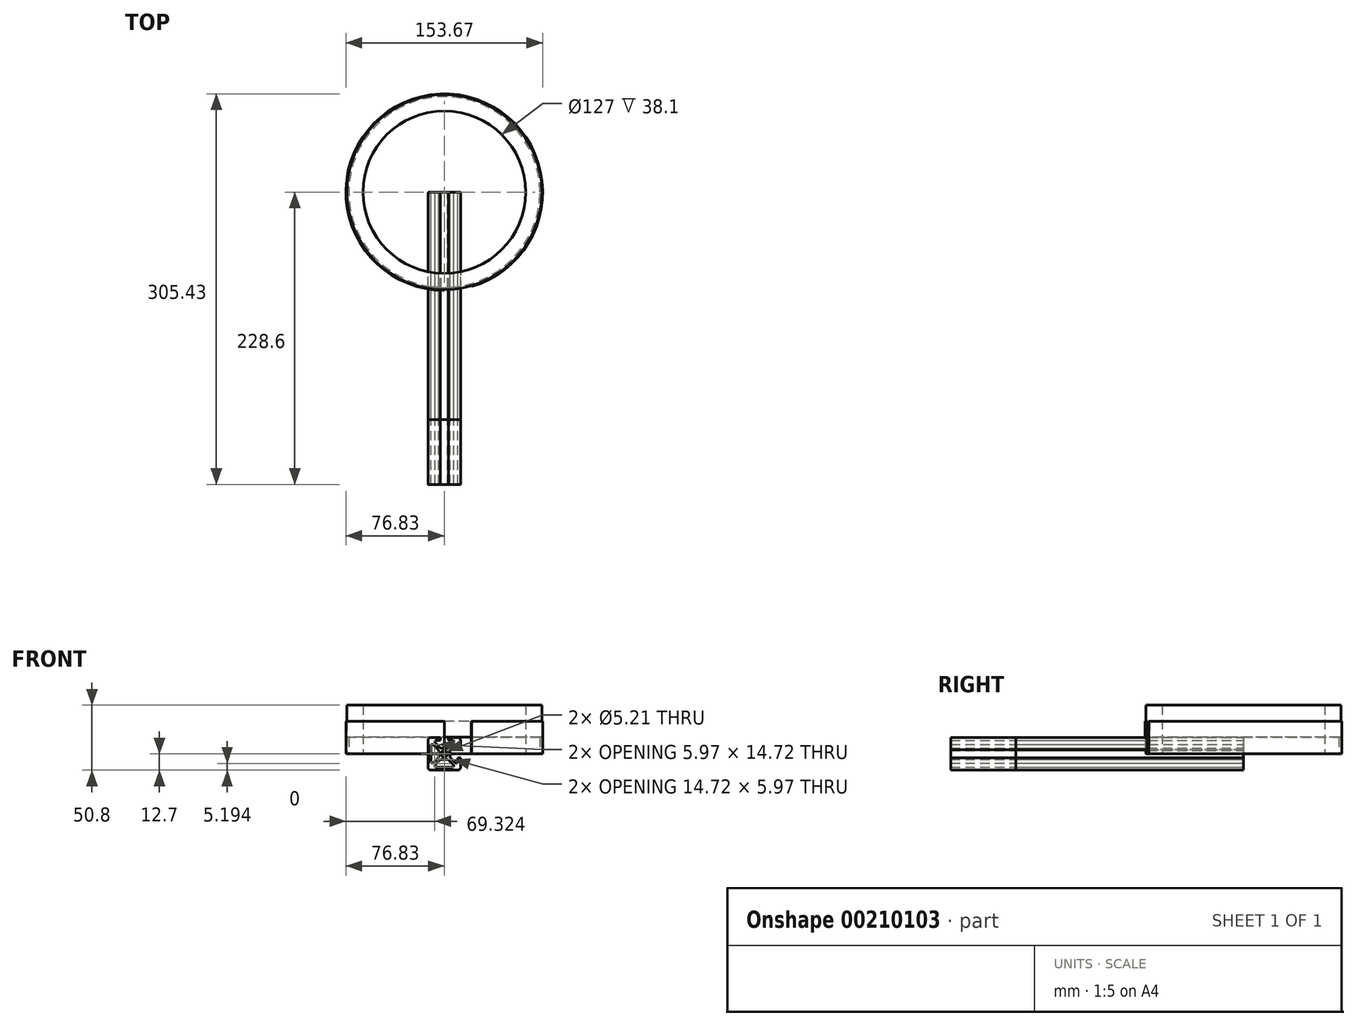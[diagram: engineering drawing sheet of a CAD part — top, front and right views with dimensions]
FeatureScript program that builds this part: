
annotation { "Feature Type Name" : "Feature", "Feature Type Description" : "" }
export const myFeature = defineFeature(function(context is Context, id is Id, definition is map)
    precondition{}
    {
        {
            var Q0;
            Q0=qCreatedBy(makeId("Front.planeOp"),FACE);
            var sketch = newSketch(context, id + "F0", { "sketchPlane" : qUnion([Q0])});
            skLineSegment(sketch, "E0.bottom", {"start": v(10.5, 12.7) * mm, "end": v(-10.5, 12.7) * mm});
            skLineSegment(sketch, "E0.top", {"start": v(10.5, -12.7) * mm, "end": v(-10.5, -12.7) * mm});
            skLineSegment(sketch, "E0.left", {"start": v(12.7, 10.5) * mm, "end": v(12.7, -10.5) * mm});
            skLineSegment(sketch, "E0.right", {"start": v(-12.7, 10.5) * mm, "end": v(-12.7, -10.5) * mm});
            skPoint(sketch, "E0.middle", {"position": v(0, 0) * mm});
            skCircle(sketch, "E1", {"center": v(0, 0) * mm, "radius": 2.6 * mm});
            skPoint(sketch, "E2.visualSharp", {"position": v(12.7, 12.7) * mm});
            skArc(sketch, "E2.filletArc", {"start": v(12.7, 10.5) * mm, "mid": v(12.05, 12.05) * mm, "end": v(10.5, 12.7) * mm});
            skPoint(sketch, "E3.visualSharp", {"position": v(-12.7, 12.7) * mm});
            skArc(sketch, "E3.filletArc", {"start": v(-10.5, 12.7) * mm, "mid": v(-12.05, 12.05) * mm, "end": v(-12.7, 10.5) * mm});
            skPoint(sketch, "E4.visualSharp", {"position": v(-12.7, -12.7) * mm});
            skArc(sketch, "E4.filletArc", {"start": v(-12.7, -10.5) * mm, "mid": v(-12.05, -12.05) * mm, "end": v(-10.5, -12.7) * mm});
            skPoint(sketch, "E5.visualSharp", {"position": v(12.7, -12.7) * mm});
            skArc(sketch, "E5.filletArc", {"start": v(10.5, -12.7) * mm, "mid": v(12.05, -12.05) * mm, "end": v(12.7, -10.5) * mm});
            skLineSegment(sketch, "E6.0", {"start": v(-3.28, 4.84) * mm, "end": v(-7.04, 8.6) * mm});
            skLineSegment(sketch, "E7", {"start": v(-2.5, 4.52) * mm, "end": v(2.5, 4.52) * mm});
            skLineSegment(sketch, "E8.MirrorCS", {"start": v(3.28, 4.84) * mm, "end": v(7.04, 8.6) * mm});
            skLineSegment(sketch, "E9", {"start": v(-6.26, 10.5) * mm, "end": v(6.26, 10.5) * mm});
            skPoint(sketch, "E10.newPointA", {"position": v(-7.42, 10.5) * mm});
            skPoint(sketch, "E10.newPointB", {"position": v(-9.7, 11.27) * mm});
            skArc(sketch, "E10.filletArc", {"start": v(-6.26, 10.5) * mm, "mid": v(-7.28, 9.8) * mm, "end": v(-7.04, 8.6) * mm});
            skPoint(sketch, "E11.newPointA", {"position": v(7.42, 10.5) * mm});
            skPoint(sketch, "E11.newPointB", {"position": v(9.7, 11.27) * mm});
            skArc(sketch, "E11.filletArc", {"start": v(7.04, 8.6) * mm, "mid": v(7.28, 9.8) * mm, "end": v(6.26, 10.5) * mm});
            skPoint(sketch, "E12.newPointA", {"position": v(-4.52, 4.52) * mm});
            skPoint(sketch, "E12.newPointB", {"position": v(0.78, 0.78) * mm});
            skArc(sketch, "E12.filletArc", {"start": v(-3.28, 4.84) * mm, "mid": v(-2.92, 4.6) * mm, "end": v(-2.5, 4.52) * mm});
            skPoint(sketch, "E13.newPointA", {"position": v(4.52, 4.52) * mm});
            skPoint(sketch, "E13.newPointB", {"position": v(-0.78, 0.78) * mm});
            skArc(sketch, "E13.filletArc", {"start": v(2.5, 4.52) * mm, "mid": v(2.92, 4.6) * mm, "end": v(3.28, 4.84) * mm});
            skArc(sketch, "E14.1.0", {"start": v(-10.5, -6.26) * mm, "mid": v(-9.8, -7.28) * mm, "end": v(-8.6, -7.04) * mm});
            skPoint(sketch, "E14.1.1", {"position": v(-10.5, -7.42) * mm});
            skPoint(sketch, "E14.1.3", {"position": v(-4.52, -4.52) * mm});
            skArc(sketch, "E14.1.4", {"start": v(-4.84, -3.28) * mm, "mid": v(-4.6, -2.92) * mm, "end": v(-4.52, -2.5) * mm});
            skLineSegment(sketch, "E14.1.5", {"start": v(-4.52, -2.5) * mm, "end": v(-4.52, 2.5) * mm});
            skLineSegment(sketch, "E14.1.6", {"start": v(-4.84, -3.28) * mm, "end": v(-8.6, -7.04) * mm});
            skArc(sketch, "E14.1.7", {"start": v(-8.6, 7.04) * mm, "mid": v(-9.8, 7.28) * mm, "end": v(-10.5, 6.26) * mm});
            skArc(sketch, "E14.1.8", {"start": v(-4.52, 2.5) * mm, "mid": v(-4.6, 2.92) * mm, "end": v(-4.84, 3.28) * mm});
            skLineSegment(sketch, "E14.1.9", {"start": v(-10.5, -6.26) * mm, "end": v(-10.5, 6.26) * mm});
            skLineSegment(sketch, "E14.1.10", {"start": v(-4.84, 3.28) * mm, "end": v(-8.6, 7.04) * mm});
            skPoint(sketch, "E14.1.11", {"position": v(-10.5, 7.42) * mm});
            skArc(sketch, "E14.2.0", {"start": v(6.26, -10.5) * mm, "mid": v(7.28, -9.8) * mm, "end": v(7.04, -8.6) * mm});
            skPoint(sketch, "E14.2.1", {"position": v(7.42, -10.5) * mm});
            skPoint(sketch, "E14.2.2", {"position": v(-4.52, -4.52) * mm});
            skPoint(sketch, "E14.2.3", {"position": v(4.52, -4.52) * mm});
            skArc(sketch, "E14.2.4", {"start": v(3.28, -4.84) * mm, "mid": v(2.92, -4.6) * mm, "end": v(2.5, -4.52) * mm});
            skLineSegment(sketch, "E14.2.5", {"start": v(2.5, -4.52) * mm, "end": v(-2.5, -4.52) * mm});
            skLineSegment(sketch, "E14.2.6", {"start": v(3.28, -4.84) * mm, "end": v(7.04, -8.6) * mm});
            skArc(sketch, "E14.2.7", {"start": v(-7.04, -8.6) * mm, "mid": v(-7.28, -9.8) * mm, "end": v(-6.26, -10.5) * mm});
            skArc(sketch, "E14.2.8", {"start": v(-2.5, -4.52) * mm, "mid": v(-2.92, -4.6) * mm, "end": v(-3.28, -4.84) * mm});
            skLineSegment(sketch, "E14.2.9", {"start": v(6.26, -10.5) * mm, "end": v(-6.26, -10.5) * mm});
            skLineSegment(sketch, "E14.2.10", {"start": v(-3.28, -4.84) * mm, "end": v(-7.04, -8.6) * mm});
            skPoint(sketch, "E14.2.11", {"position": v(-7.42, -10.5) * mm});
            skArc(sketch, "E14.3.0", {"start": v(10.5, 6.26) * mm, "mid": v(9.8, 7.28) * mm, "end": v(8.6, 7.04) * mm});
            skPoint(sketch, "E14.3.1", {"position": v(10.5, 7.42) * mm});
            skPoint(sketch, "E14.3.2", {"position": v(4.52, -4.52) * mm});
            skArc(sketch, "E14.3.4", {"start": v(4.84, 3.28) * mm, "mid": v(4.6, 2.92) * mm, "end": v(4.52, 2.5) * mm});
            skLineSegment(sketch, "E14.3.5", {"start": v(4.52, 2.5) * mm, "end": v(4.52, -2.5) * mm});
            skLineSegment(sketch, "E14.3.6", {"start": v(4.84, 3.28) * mm, "end": v(8.6, 7.04) * mm});
            skArc(sketch, "E14.3.7", {"start": v(8.6, -7.04) * mm, "mid": v(9.8, -7.28) * mm, "end": v(10.5, -6.26) * mm});
            skArc(sketch, "E14.3.8", {"start": v(4.52, -2.5) * mm, "mid": v(4.6, -2.92) * mm, "end": v(4.84, -3.28) * mm});
            skLineSegment(sketch, "E14.3.9", {"start": v(10.5, 6.26) * mm, "end": v(10.5, -6.26) * mm});
            skLineSegment(sketch, "E14.3.10", {"start": v(4.84, -3.28) * mm, "end": v(8.6, -7.04) * mm});
            skPoint(sketch, "E14.3.11", {"position": v(10.5, -7.42) * mm});
            skLineSegment(sketch, "E15.bottom", {"start": v(3.25, 17.01) * mm, "end": v(-3.25, 17.01) * mm});
            skLineSegment(sketch, "E15.top", {"start": v(3.25, 8.39) * mm, "end": v(-3.25, 8.39) * mm});
            skLineSegment(sketch, "E15.left", {"start": v(3.25, 17.01) * mm, "end": v(3.25, 8.39) * mm});
            skLineSegment(sketch, "E15.right", {"start": v(-3.25, 17.01) * mm, "end": v(-3.25, 8.39) * mm});
            skPoint(sketch, "E15.middle", {"position": v(0, 12.7) * mm});
            skLineSegment(sketch, "E16.bottom", {"start": v(7.75, -3.25) * mm, "end": v(17.65, -3.25) * mm});
            skLineSegment(sketch, "E16.top", {"start": v(7.75, 3.25) * mm, "end": v(17.65, 3.25) * mm});
            skLineSegment(sketch, "E16.left", {"start": v(7.75, -3.25) * mm, "end": v(7.75, 3.25) * mm});
            skLineSegment(sketch, "E16.right", {"start": v(17.65, -3.25) * mm, "end": v(17.65, 3.25) * mm});
            skPoint(sketch, "E16.middle", {"position": v(12.7, 0) * mm});
            skSolve(sketch);
        }
        {
            var Q0;
            Q0=makeQuery(id+"F0.imprint","IMPRINT",FACE,{"disambiguationData":[TD([[makeQuery(id+"F0.imprint","IMPRINT",EDGE,{"derivedFrom":sQuery(id+"F0.wireOp",EDGE,"E0.bottom")}),1.0]])]});
            extrude(context, id + "F1", {"entities" : qUnion([Q0]), "depth" : 228.6 * mm});
        }
        {
            var Q0;
            Q0=qCreatedBy(makeId("Front.planeOp"),FACE);
            var sketch = newSketch(context, id + "F2", { "sketchPlane" : qUnion([Q0])});
            skLineSegment(sketch, "E17.bottom", {"start": v(10.5, 12.7) * mm, "end": v(-10.5, 12.7) * mm});
            skLineSegment(sketch, "E17.top", {"start": v(10.5, -12.7) * mm, "end": v(-10.5, -12.7) * mm});
            skLineSegment(sketch, "E17.left", {"start": v(12.7, 10.5) * mm, "end": v(12.7, -10.5) * mm});
            skLineSegment(sketch, "E17.right", {"start": v(-12.7, 10.5) * mm, "end": v(-12.7, -10.5) * mm});
            skPoint(sketch, "E17.middle", {"position": v(0, 0) * mm});
            skCircle(sketch, "E18", {"center": v(0, 0) * mm, "radius": 2.6 * mm});
            skPoint(sketch, "E19.visualSharp", {"position": v(12.7, 12.7) * mm});
            skArc(sketch, "E19.filletArc", {"start": v(12.7, 10.5) * mm, "mid": v(12.05, 12.05) * mm, "end": v(10.5, 12.7) * mm});
            skPoint(sketch, "E20.visualSharp", {"position": v(-12.7, 12.7) * mm});
            skArc(sketch, "E20.filletArc", {"start": v(-10.5, 12.7) * mm, "mid": v(-12.05, 12.05) * mm, "end": v(-12.7, 10.5) * mm});
            skPoint(sketch, "E21.visualSharp", {"position": v(-12.7, -12.7) * mm});
            skArc(sketch, "E21.filletArc", {"start": v(-12.7, -10.5) * mm, "mid": v(-12.05, -12.05) * mm, "end": v(-10.5, -12.7) * mm});
            skPoint(sketch, "E22.visualSharp", {"position": v(12.7, -12.7) * mm});
            skArc(sketch, "E22.filletArc", {"start": v(10.5, -12.7) * mm, "mid": v(12.05, -12.05) * mm, "end": v(12.7, -10.5) * mm});
            skSolve(sketch);
        }
        {
            var Q0;
            Q0=makeQuery(id+"F2.imprint","IMPRINT",FACE,{"disambiguationData":[TD([[makeQuery(id+"F2.imprint","IMPRINT",EDGE,{"derivedFrom":sQuery(id+"F2.wireOp",EDGE,"E17.bottom")}),1.0]])]});
            extrude(context, id + "F3", {"entities" : qUnion([Q0]), "depth" : 177.8 * mm});
        }
        {
            var Q0;
            Q0=makeQuery(id+"F0.imprint","IMPRINT",FACE,{"disambiguationData":[TD([[makeQuery(id+"F0.imprint","IMPRINT",EDGE,{"derivedFrom":sQuery(id+"F0.wireOp",EDGE,"E6.0")}),-1.0]])]});
            var Q1;
            Q1=makeQuery(id+"F0.imprint","IMPRINT",FACE,{"disambiguationData":[TD([[makeQuery(id+"F0.imprint","IMPRINT",EDGE,{"derivedFrom":sQuery(id+"F0.wireOp",EDGE,"E14.1.0")}),1.0]])]});
            var Q2;
            Q2=makeQuery(id+"F0.imprint","IMPRINT",FACE,{"disambiguationData":[TD([[makeQuery(id+"F0.imprint","IMPRINT",EDGE,{"derivedFrom":sQuery(id+"F0.wireOp",EDGE,"E14.3.0")}),1.0]])]});
            var Q3;
            Q3=makeQuery(id+"F0.imprint","IMPRINT",FACE,{"disambiguationData":[TD([[makeQuery(id+"F0.imprint","IMPRINT",EDGE,{"derivedFrom":sQuery(id+"F0.wireOp",EDGE,"E14.2.0")}),1.0]])]});
            extrude(context, id + "F4", {"entities" : qUnion([Q0, Q1, Q2, Q3]), "operationType" : NewBodyOperationType.REMOVE, "endBound" : BoundingType.THROUGH_ALL, "depth" : 25.4 * mm});
        }
        {
            var Q0;
            {var subQ0=sQuery(id+"F0.wireOp",EDGE,"E15.left");var subQ1=sQuery(id+"F0.wireOp",EDGE,"E0.bottom");var subQ2=makeQuery(id+"F0.imprint","INTERSECT",VERTEX,{"derivedFrom":[subQ1,subQ0]});Q0=makeQuery(id+"F0.imprint","IMPRINT",FACE,{"disambiguationData":[TD([[makeQuery(id+"F0.imprint","IMPRINT",EDGE,{"disambiguationData":[TD([[subQ2,-1.0]])],"derivedFrom":subQ1}),1.0]])]});}
            var Q1;
            {var subQ5=sQuery(id+"F0.wireOp",EDGE,"E15.top");Q1=makeQuery(id+"F0.imprint","IMPRINT",FACE,{"disambiguationData":[TD([[makeQuery(id+"F0.imprint","IMPRINT",EDGE,{"derivedFrom":subQ5}),-1.0]])]});}
            var Q2;
            {var subQ5=sQuery(id+"F0.wireOp",EDGE,"E15.bottom");Q2=makeQuery(id+"F0.imprint","IMPRINT",FACE,{"disambiguationData":[TD([[makeQuery(id+"F0.imprint","IMPRINT",EDGE,{"derivedFrom":subQ5}),1.0]])]});}
            extrude(context, id + "F5", {"entities" : qUnion([Q0, Q1, Q2]), "operationType" : NewBodyOperationType.REMOVE, "endBound" : BoundingType.THROUGH_ALL, "depth" : 25.4 * mm});
        }
        {
            var Q0;
            {var subQ5=sQuery(id+"F0.wireOp",EDGE,"E16.right");Q0=makeQuery(id+"F0.imprint","IMPRINT",FACE,{"disambiguationData":[TD([[makeQuery(id+"F0.imprint","IMPRINT",EDGE,{"derivedFrom":subQ5}),1.0]])]});}
            var Q1;
            {var subQ0=sQuery(id+"F0.wireOp",EDGE,"E16.top");var subQ1=sQuery(id+"F0.wireOp",EDGE,"E0.left");var subQ2=makeQuery(id+"F0.imprint","INTERSECT",VERTEX,{"derivedFrom":[subQ1,subQ0]});Q1=makeQuery(id+"F0.imprint","IMPRINT",FACE,{"disambiguationData":[TD([[makeQuery(id+"F0.imprint","IMPRINT",EDGE,{"disambiguationData":[TD([[subQ2,-1.0]])],"derivedFrom":subQ1}),-1.0]])]});}
            var Q2;
            {var subQ5=sQuery(id+"F0.wireOp",EDGE,"E16.left");Q2=makeQuery(id+"F0.imprint","IMPRINT",FACE,{"disambiguationData":[TD([[makeQuery(id+"F0.imprint","IMPRINT",EDGE,{"derivedFrom":subQ5}),-1.0]])]});}
            extrude(context, id + "F6", {"entities" : qUnion([Q0, Q1, Q2]), "operationType" : NewBodyOperationType.REMOVE, "endBound" : BoundingType.THROUGH_ALL, "depth" : 25.4 * mm});
        }
        {
            var Q0;
            Q0=makeQuery(id+"F5.boolean.opBoolean","INTERSECT",EDGE,{"derivedFrom":[makeQuery(id+"F3.opExtrude","SWEPT_FACE",FACE,{"disambiguationData":[OSD([sQuery(id+"F2.wireOp",EDGE,"E17.bottom")])]}),makeQuery(id+"F5.opExtrude","SWEPT_FACE",FACE,{"disambiguationData":[OSD([sQuery(id+"F0.wireOp",EDGE,"E15.right")])]})]});
            var Q1;
            Q1=makeQuery(id+"F4.boolean.opBoolean","COPY",EDGE,{"derivedFrom":makeQuery(id+"F4.opExtrude","SWEPT_EDGE",EDGE,{"disambiguationData":[OSD([sQuery(id+"F0.wireOp",EDGE,"E9"),sQuery(id+"F0.wireOp",EDGE,"E15.right")])]})});
            var Q2;
            Q2=makeQuery(id+"F5.boolean.opBoolean","INTERSECT",EDGE,{"derivedFrom":[makeQuery(id+"F3.opExtrude","SWEPT_FACE",FACE,{"disambiguationData":[OSD([sQuery(id+"F2.wireOp",EDGE,"E17.bottom")])]}),makeQuery(id+"F5.opExtrude","SWEPT_FACE",FACE,{"disambiguationData":[OSD([sQuery(id+"F0.wireOp",EDGE,"E15.left")])]})]});
            var Q3;
            Q3=makeQuery(id+"F6.boolean.opBoolean","INTERSECT",EDGE,{"derivedFrom":[makeQuery(id+"F3.opExtrude","SWEPT_FACE",FACE,{"disambiguationData":[OSD([sQuery(id+"F2.wireOp",EDGE,"E17.left")])]}),makeQuery(id+"F6.opExtrude","SWEPT_FACE",FACE,{"disambiguationData":[OSD([sQuery(id+"F0.wireOp",EDGE,"E16.top")])]})]});
            var Q4;
            Q4=makeQuery(id+"F6.boolean.opBoolean","INTERSECT",EDGE,{"derivedFrom":[makeQuery(id+"F3.opExtrude","SWEPT_FACE",FACE,{"disambiguationData":[OSD([sQuery(id+"F2.wireOp",EDGE,"E17.left")])]}),makeQuery(id+"F6.opExtrude","SWEPT_FACE",FACE,{"disambiguationData":[OSD([sQuery(id+"F0.wireOp",EDGE,"E16.bottom")])]})]});
            var Q5;
            Q5=makeQuery(id+"F4.boolean.opBoolean","COPY",EDGE,{"derivedFrom":makeQuery(id+"F4.opExtrude","SWEPT_EDGE",EDGE,{"disambiguationData":[OSD([sQuery(id+"F0.wireOp",EDGE,"E14.3.9"),sQuery(id+"F0.wireOp",EDGE,"E16.bottom")])]})});
            var Q6;
            Q6=makeQuery(id+"F4.boolean.opBoolean","COPY",EDGE,{"derivedFrom":makeQuery(id+"F4.opExtrude","SWEPT_EDGE",EDGE,{"disambiguationData":[OSD([sQuery(id+"F0.wireOp",EDGE,"E9"),sQuery(id+"F0.wireOp",EDGE,"E15.left")])]})});
            var Q7;
            Q7=makeQuery(id+"F4.boolean.opBoolean","COPY",EDGE,{"derivedFrom":makeQuery(id+"F4.opExtrude","SWEPT_EDGE",EDGE,{"disambiguationData":[OSD([sQuery(id+"F0.wireOp",EDGE,"E14.3.9"),sQuery(id+"F0.wireOp",EDGE,"E16.top")])]})});
            fillet(context, id + "F7", {"entities" : qUnion([Q0, Q1, Q2, Q3, Q4, Q5, Q6, Q7]), "radius" : 1.1 * mm, "tangentPropagation" : true, "allowEdgeOverflow" : false});
        }
        {
            var Q0;
            Q0=qCreatedBy(makeId("Top.planeOp"),FACE);
            var sketch = newSketch(context, id + "F8", { "sketchPlane" : qUnion([Q0])});
            skCircle(sketch, "E23", {"center": v(0, 0) * mm, "radius": 63.5 * mm});
            skCircle(sketch, "E24", {"center": v(0, 0) * mm, "radius": 76.2 * mm});
            skSolve(sketch);
        }
        {
            var Q0;
            Q0 = qSketchRegion(id + "F8", true);
            extrude(context, id + "F9", {"entities" : qUnion([Q0]), "depth" : 38.1 * mm});
        }
        {
            var Q0;
            Q0=qCreatedBy(makeId("Top.planeOp"),FACE);
            var sketch = newSketch(context, id + "F10", { "sketchPlane" : qUnion([Q0])});
            skCircle(sketch, "E25", {"center": v(0, 0) * mm, "radius": 74.61 * mm});
            skCircle(sketch, "E26", {"center": v(0, 0) * mm, "radius": 76.2 * mm});
            skSolve(sketch);
        }
        {
            var Q0;
            Q0 = qSketchRegion(id + "F10", true);
            extrude(context, id + "F11", {"entities" : qUnion([Q0]), "operationType" : NewBodyOperationType.REMOVE, "depth" : 12.95 * mm});
        }
        {
            var Q0;
            Q0=qCreatedBy(makeId("Top.planeOp"),FACE);
            var sketch = newSketch(context, id + "F12", { "sketchPlane" : qUnion([Q0])});
            skArc(sketch, "E27", {"start": v(21, -73.25) * mm, "mid": v(-10.6, 75.46) * mm, "end": v(0, -76.2) * mm});
            skArc(sketch, "E28", {"start": v(21.18, -73.86) * mm, "mid": v(-10.7, 76.09) * mm, "end": v(0, -76.83) * mm});
            skLineSegment(sketch, "E29", {"start": v(0, -76.2) * mm, "end": v(0, -76.83) * mm});
            skLineSegment(sketch, "E30", {"start": v(21, -73.25) * mm, "end": v(21.18, -73.86) * mm});
            skSolve(sketch);
        }
        {
            var Q0;
            Q0 = qSketchRegion(id + "F12", true);
            extrude(context, id + "F13", {"entities" : qUnion([Q0]), "depth" : 25.4 * mm});
        }
    });
